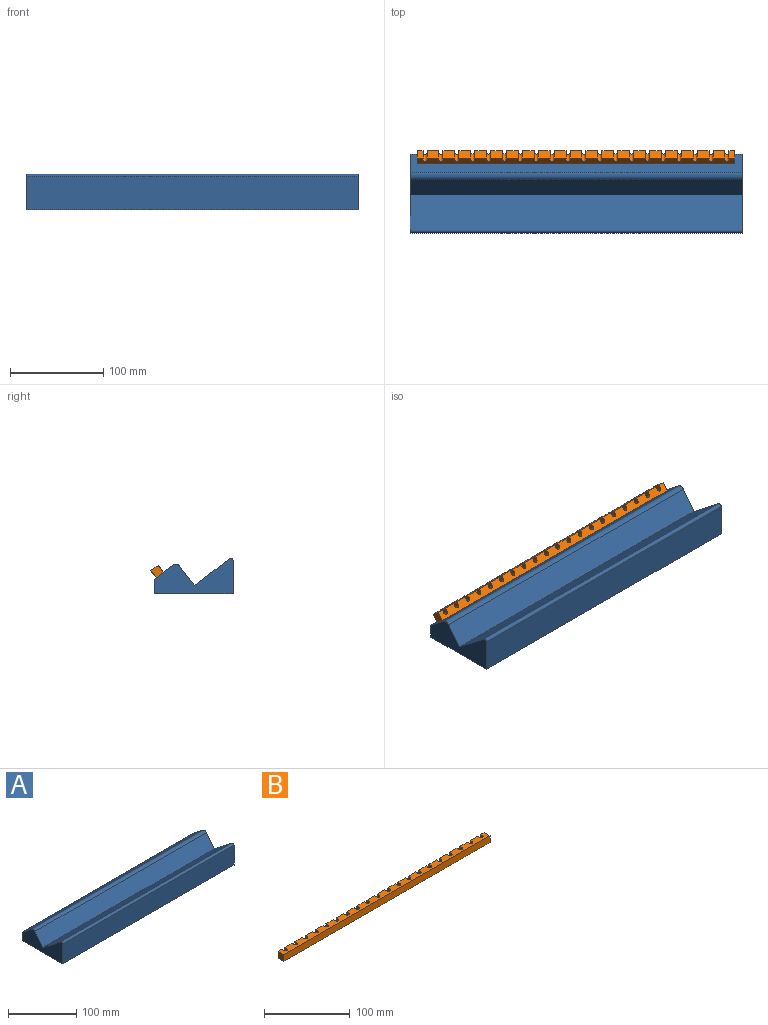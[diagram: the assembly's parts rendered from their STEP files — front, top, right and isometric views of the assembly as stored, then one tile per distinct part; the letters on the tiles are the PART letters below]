
ASSEMBLY  parts=2 mates=1
PART A: 10 faces, bbox 355.6x84.3x38 mm
  f0: plane 355.6x37.11mm, normal (0,0.61,0.79), area 16702.5mm2, adj f5,f6,f7,f8
  f1: plane 355.6x35.46mm, normal (0,-1,0), area 12607.9mm2, adj f2,f6,f7,f8
  f2: plane 355.6x84.33mm, normal (0,0,-1), area 29987mm2, adj f1,f3,f6,f7
  f3: plane 355.6x15.24mm, normal (0,1,0), area 5419.3mm2, adj f2,f4,f6,f7
  f4: plane 355.6x19.73mm, normal (0,0.61,0.79), area 8877.7mm2, adj f3,f6,f7,f9
  f5: plane 355.6x20.97mm, normal (0,-0.79,0.61), area 9435.9mm2, adj f0,f6,f7,f9
  f6: plane 84.33x38mm, normal (-1,0,0), area 1995.1mm2, adj f0,f1,f2,f3,f4,f5,f8,f9
  f7: plane 84.33x38mm, normal (1,0,0), area 1995.1mm2, adj f0,f1,f2,f3,f4,f5,f8,f9
  f8: cylinder r=2.54mm len=355.6mm, axis (1,0,0), area 2014.7mm2, adj f0,f1,f6,f7
  f9: cylinder r=5.08mm len=355.6mm, axis (1,0,0), area 2837.6mm2, adj f4,f5,f6,f7
PART B: 46 faces, bbox 340.4x9.7x9.7 mm
  f0: extruded ~9.65x5.84mm, area 136.6mm2, adj f1,f43,f44,f45
  f1: plane 12.7x9.65mm, normal (0,1,0), area 122.6mm2, adj f0,f2,f44,f45
  f2: extruded ~9.65x5.84mm, area 136.6mm2, adj f1,f3,f44,f45
  f3: plane 12.7x9.65mm, normal (0,1,0), area 122.6mm2, adj f2,f4,f44,f45
  f4: extruded ~9.65x5.84mm, area 136.6mm2, adj f3,f5,f44,f45
  f5: plane 12.7x9.65mm, normal (0,1,0), area 122.6mm2, adj f4,f6,f44,f45
  f6: extruded ~9.65x5.84mm, area 136.6mm2, adj f5,f7,f44,f45
  f7: plane 12.7x9.65mm, normal (0,1,0), area 122.6mm2, adj f6,f8,f44,f45
  f8: extruded ~9.65x5.84mm, area 136.6mm2, adj f7,f9,f44,f45
  f9: plane 12.7x9.65mm, normal (0,1,0), area 122.6mm2, adj f8,f10,f44,f45
  f10: extruded ~9.65x5.84mm, area 136.6mm2, adj f9,f11,f44,f45
  f11: plane 12.7x9.65mm, normal (0,1,0), area 122.6mm2, adj f10,f12,f44,f45
  f12: extruded ~9.65x5.84mm, area 136.6mm2, adj f11,f13,f44,f45
  f13: plane 12.7x9.65mm, normal (0,1,0), area 122.6mm2, adj f12,f14,f44,f45
  f14: extruded ~9.65x5.84mm, area 136.6mm2, adj f13,f15,f44,f45
  f15: plane 12.7x9.65mm, normal (0,1,0), area 122.6mm2, adj f14,f16,f44,f45
  f16: extruded ~9.65x5.84mm, area 136.6mm2, adj f15,f17,f44,f45
  f17: plane 12.7x9.65mm, normal (0,1,0), area 122.6mm2, adj f16,f18,f44,f45
  f18: extruded ~9.65x5.84mm, area 136.6mm2, adj f17,f19,f44,f45
  f19: plane 12.7x9.65mm, normal (0,1,0), area 122.6mm2, adj f18,f20,f44,f45
  f20: extruded ~9.65x5.84mm, area 136.6mm2, adj f19,f21,f44,f45
  f21: plane 12.7x9.65mm, normal (0,1,0), area 122.6mm2, adj f20,f22,f44,f45
  f22: extruded ~9.65x5.84mm, area 136.6mm2, adj f21,f23,f44,f45
  f23: plane 12.7x9.65mm, normal (0,1,0), area 122.6mm2, adj f22,f24,f44,f45
  f24: extruded ~9.65x5.84mm, area 136.6mm2, adj f23,f25,f44,f45
  f25: plane 9.65x6.35mm, normal (0,1,0), area 61.3mm2, adj f24,f26,f44,f45
  f26: plane 9.65x9.65mm, normal (-1,0,0), area 93.2mm2, adj f25,f27,f44,f45
  f27: plane 340.36x9.65mm, normal (0,-1,0), area 3285.2mm2, adj f26,f28,f44,f45
  f28: plane 9.65x9.65mm, normal (1,0,0), area 93.2mm2, adj f27,f29,f44,f45
  f29: plane 9.65x6.35mm, normal (0,1,0), area 61.3mm2, adj f28,f30,f44,f45
  f30: extruded ~9.65x5.84mm, area 136.6mm2, adj f29,f31,f44,f45
  f31: plane 12.7x9.65mm, normal (0,1,0), area 122.6mm2, adj f30,f32,f44,f45
  f32: extruded ~9.65x5.84mm, area 136.6mm2, adj f31,f33,f44,f45
  f33: plane 12.7x9.65mm, normal (0,1,0), area 122.6mm2, adj f32,f34,f44,f45
  f34: extruded ~9.65x5.84mm, area 136.6mm2, adj f33,f35,f44,f45
  f35: plane 12.7x9.65mm, normal (0,1,0), area 122.6mm2, adj f34,f36,f44,f45
  f36: extruded ~9.65x5.84mm, area 136.6mm2, adj f35,f37,f44,f45
  f37: plane 12.7x9.65mm, normal (0,1,0), area 122.6mm2, adj f36,f38,f44,f45
  f38: extruded ~9.65x5.84mm, area 136.6mm2, adj f37,f39,f44,f45
  f39: plane 12.7x9.65mm, normal (0,1,0), area 122.6mm2, adj f38,f40,f44,f45
  f40: extruded ~9.65x5.84mm, area 136.6mm2, adj f39,f41,f44,f45
  f41: plane 12.7x9.65mm, normal (0,1,0), area 122.6mm2, adj f40,f42,f44,f45
  f42: extruded ~9.65x5.84mm, area 136.6mm2, adj f41,f43,f44,f45
  f43: plane 12.7x9.65mm, normal (0,1,0), area 122.6mm2, adj f0,f42,f44,f45
  f44: plane 340.36x9.65mm, normal (0,0,-1), area 2800mm2, adj f0,f1,f2,f3,f4,f5,f6,f7
  f45: plane 340.36x9.65mm, normal (0,0,1), area 2800mm2, adj f0,f1,f2,f3,f4,f5,f6,f7
PLACE A t=(-40.97,-55.37,24.16)mm
PLACE B rot(axis=(1,0,0),52.2deg) t=(-48.59,-65.24,47.05)mm
MATE planar B.f27 <-> A.f4  axis (0,-0.61,-0.79) through (-218.77,-65.24,47.05)mm
